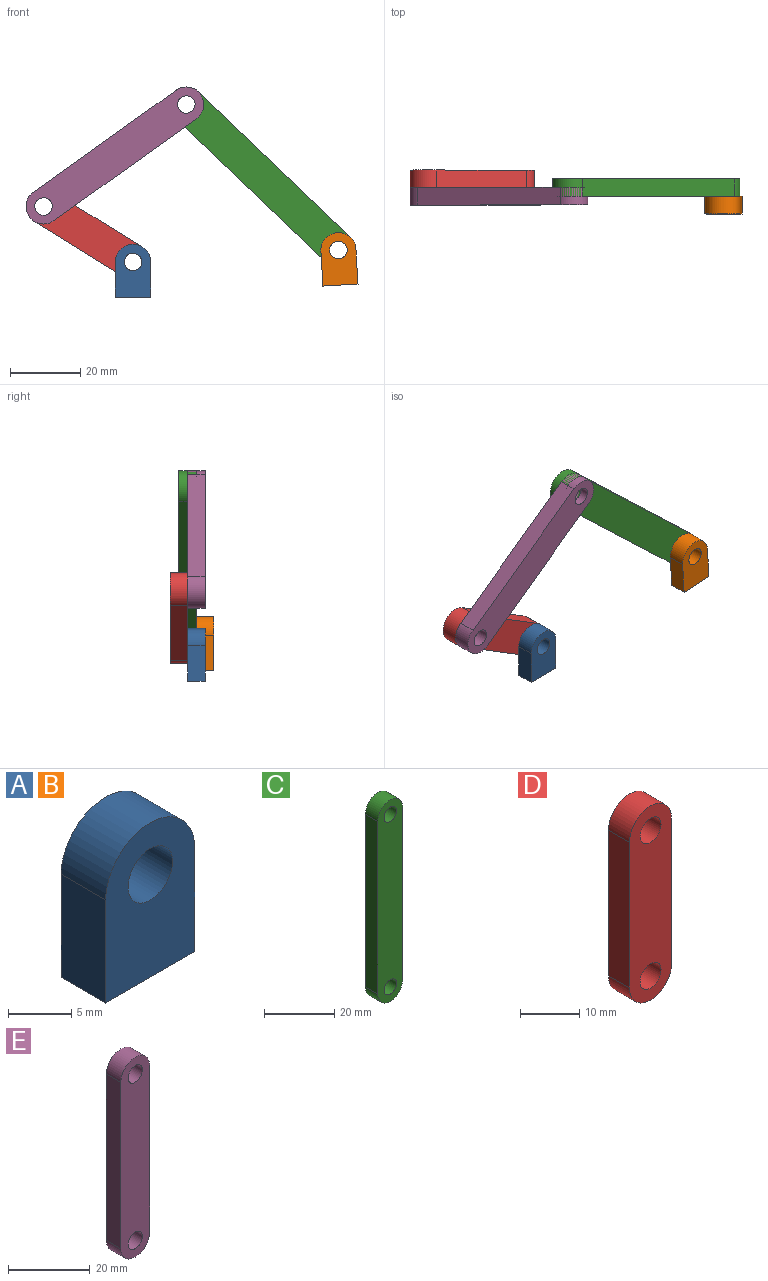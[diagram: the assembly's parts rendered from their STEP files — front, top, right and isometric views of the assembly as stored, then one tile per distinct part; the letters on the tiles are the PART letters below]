
ASSEMBLY  parts=5 mates=4
PART A: 7 faces, bbox 10x5x15 mm
  f0: plane 10x5mm, normal (1,0,0), area 50mm2, adj f1,f3,f5,f6
  f1: cylinder r=5mm len=10mm, axis (0,1,0), area 78.5mm2, adj f0,f2,f5,f6
  f2: plane 10x5mm, normal (-1,0,0), area 50mm2, adj f1,f3,f5,f6
  f3: plane 10x5mm, normal (0,0,-1), area 50mm2, adj f0,f2,f5,f6
  f4: cylinder r=2.5mm len=5mm, axis (0,1,0), area 78.5mm2, adj f5,f6
  f5: plane 15x10mm, normal (0,-1,0), area 119.6mm2, adj f0,f1,f2,f3,f4
  f6: plane 15x10mm, normal (0,1,0), area 119.6mm2, adj f0,f1,f2,f3,f4
PART B: same geometry as A
PART C: 8 faces, bbox 10x5x70 mm
  f0: plane 60x5mm, normal (1,0,0), area 300mm2, adj f1,f5,f6,f7
  f1: cylinder r=5mm len=10mm, axis (0,1,0), area 78.5mm2, adj f0,f2,f6,f7
  f2: plane 60x5mm, normal (-1,0,0), area 300mm2, adj f1,f5,f6,f7
  f3: cylinder r=2.5mm len=5mm, axis (0,1,0), area 78.5mm2, adj f6,f7
  f4: cylinder r=2.5mm len=5mm, axis (0,1,0), area 78.5mm2, adj f6,f7
  f5: cylinder r=5mm len=10mm, axis (0,1,0), area 78.5mm2, adj f0,f2,f6,f7
  f6: plane 70x10mm, normal (0,-1,0), area 639.3mm2, adj f0,f1,f2,f3,f4,f5
  f7: plane 70x10mm, normal (0,1,0), area 639.3mm2, adj f0,f1,f2,f3,f4,f5
PART D: 8 faces, bbox 10x5x40 mm
  f0: plane 30x5mm, normal (1,0,0), area 150mm2, adj f1,f5,f6,f7
  f1: cylinder r=5mm len=10mm, axis (0,1,0), area 78.5mm2, adj f0,f2,f6,f7
  f2: plane 30x5mm, normal (-1,0,0), area 150mm2, adj f1,f5,f6,f7
  f3: cylinder r=2.5mm len=5mm, axis (0,1,0), area 78.5mm2, adj f6,f7
  f4: cylinder r=2.5mm len=5mm, axis (0,1,0), area 78.5mm2, adj f6,f7
  f5: cylinder r=5mm len=10mm, axis (0,1,0), area 78.5mm2, adj f0,f2,f6,f7
  f6: plane 40x10mm, normal (0,-1,0), area 339.3mm2, adj f0,f1,f2,f3,f4,f5
  f7: plane 40x10mm, normal (0,1,0), area 339.3mm2, adj f0,f1,f2,f3,f4,f5
PART E: 8 faces, bbox 10x5x60 mm
  f0: plane 50x5mm, normal (1,0,0), area 250mm2, adj f1,f5,f6,f7
  f1: cylinder r=5mm len=10mm, axis (0,1,0), area 78.5mm2, adj f0,f2,f6,f7
  f2: plane 50x5mm, normal (-1,0,0), area 250mm2, adj f1,f5,f6,f7
  f3: cylinder r=2.5mm len=5mm, axis (0,1,0), area 78.5mm2, adj f6,f7
  f4: cylinder r=2.5mm len=5mm, axis (0,1,0), area 78.5mm2, adj f6,f7
  f5: cylinder r=5mm len=10mm, axis (0,1,0), area 78.5mm2, adj f0,f2,f6,f7
  f6: plane 60x10mm, normal (0,-1,0), area 539.3mm2, adj f0,f1,f2,f3,f4,f5
  f7: plane 60x10mm, normal (0,1,0), area 539.3mm2, adj f0,f1,f2,f3,f4,f5
PLACE A t=(-5.59,2.36,-1.42)mm fixed
PLACE B rot(axis=(0,-1,0),3.4deg) t=(52.95,-0.14,1.97)mm fixed
PLACE C rot(axis=(0,-1,0),46.3deg) t=(52.95,4.86,1.97)mm
PLACE D rot(axis=(0,1,0),121.8deg) t=(-31.09,7.36,14.38)mm
PLACE E rot(axis=(0,-1,0),125.5deg) t=(9.59,2.36,43.44)mm
MATE revolute D.f1 <-> A.f1  axis (0,-1,0) through (-5.59,2.36,-1.42)mm
MATE revolute E.f4 <-> C.f1  axis (0,1,0) through (9.59,2.36,43.44)mm
MATE revolute D.f4 <-> E.f1  axis (0,-1,0) through (-31.09,2.36,14.38)mm
MATE revolute C.f3 <-> B.f1  axis (0,-1,0) through (52.95,-0.14,1.97)mm
